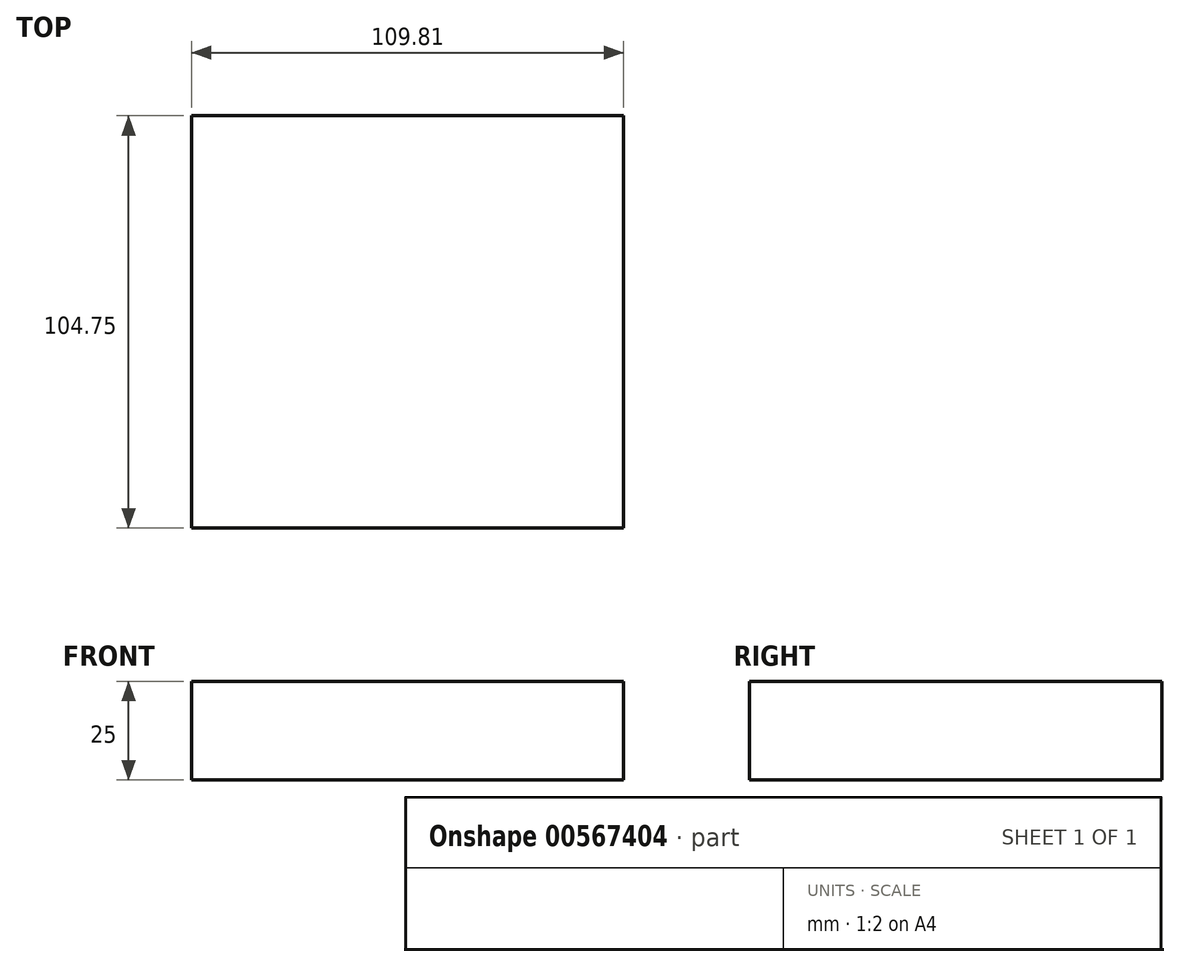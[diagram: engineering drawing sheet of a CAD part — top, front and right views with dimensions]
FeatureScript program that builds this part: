
annotation { "Feature Type Name" : "Feature", "Feature Type Description" : "" }
export const myFeature = defineFeature(function(context is Context, id is Id, definition is map)
    precondition{}
    {
        {
            var Q0;
            Q0=qCreatedBy(makeId("Top.planeOp"),FACE);
            var sketch = newSketch(context, id + "F0", { "sketchPlane" : qUnion([Q0])});
            skLineSegment(sketch, "E0.bottom", {"start": v(-55.27, 46.9) * mm, "end": v(54.54, 46.9) * mm});
            skLineSegment(sketch, "E0.top", {"start": v(-55.27, -57.84) * mm, "end": v(54.54, -57.84) * mm});
            skLineSegment(sketch, "E0.left", {"start": v(-55.27, 46.9) * mm, "end": v(-55.27, -57.84) * mm});
            skLineSegment(sketch, "E0.right", {"start": v(54.54, 46.9) * mm, "end": v(54.54, -57.84) * mm});
            skSolve(sketch);
        }
        {
            var Q0;
            Q0 = qSketchRegion(id + "F0", true);
            extrude(context, id + "F1", {"entities" : qUnion([Q0]), "depth" : 25 * mm, "offsetDistance" : 25 * mm});
        }
    });
